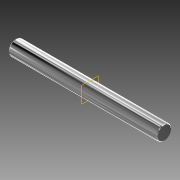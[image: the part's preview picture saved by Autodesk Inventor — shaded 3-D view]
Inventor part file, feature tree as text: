
AUTODESK INVENTOR PART (.ipt)
format: ipt  version: 2015 (Build 190159000, 159)  size: 78,336 bytes
history: native  units: mm
features: revolve x1, chamfer x1
ambient origin geometry x8: Origin, YZ Plane, XZ Plane, XY Plane, X Axis, Y Axis, Z Axis, Center Point
bodies: Solid1 (feature_tree)
feature tree (2):
  revolve  "Revolución1"  [1 undecoded]
  chamfer  "Chaflán1"  Distance=50.0mm
note: 1 required parameter value undecoded (feature->parameter linkage not recoverable at this tier; creation-order binding heuristic only, values carry confidence <= 0.55)
